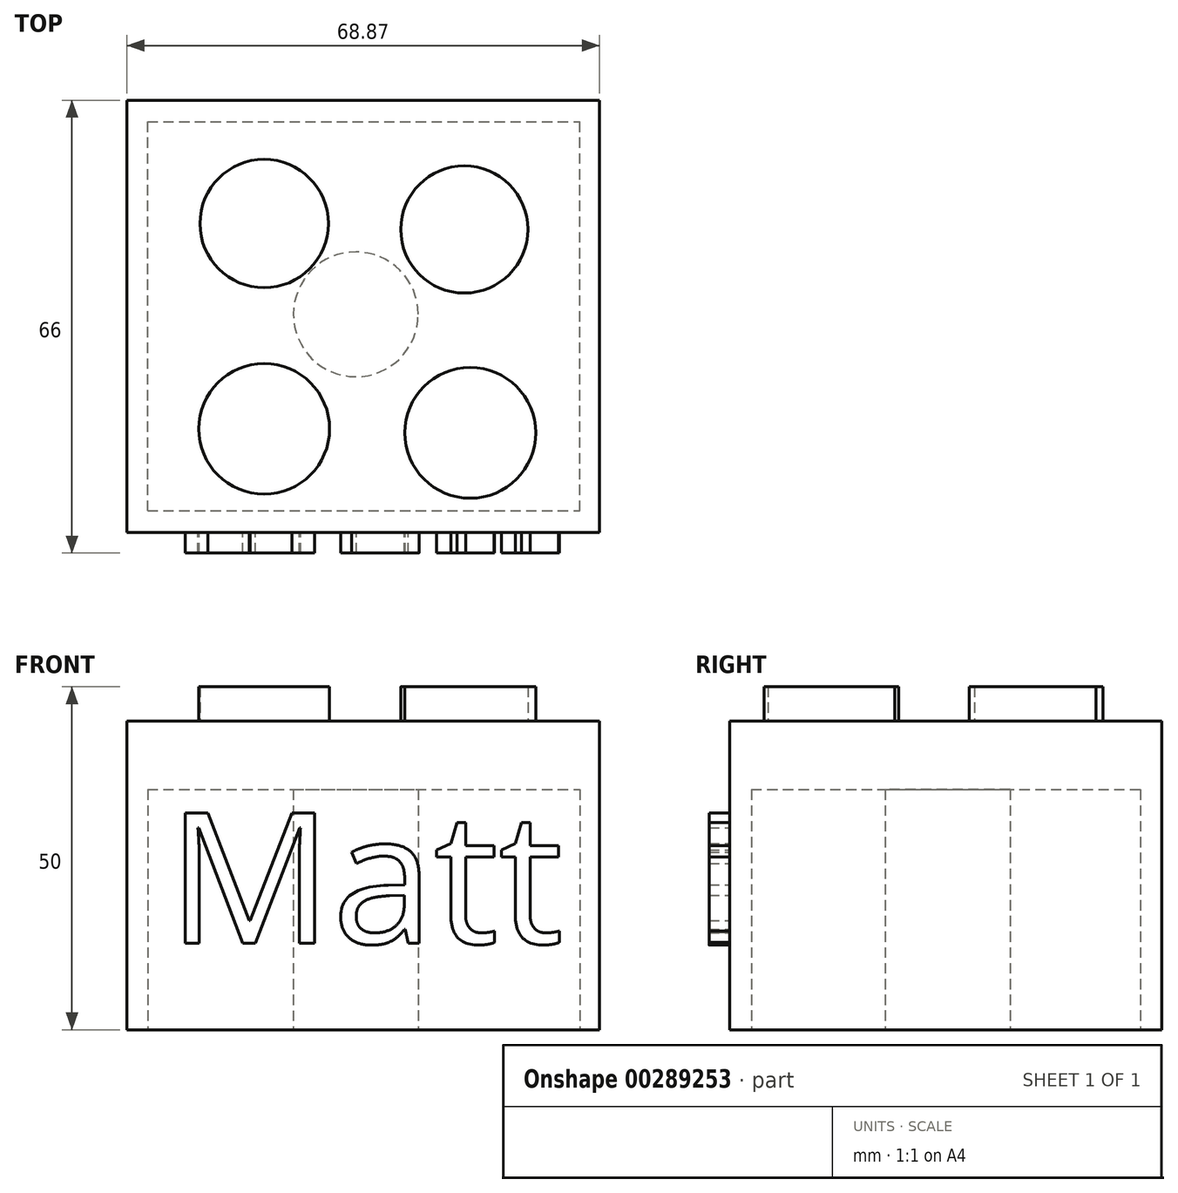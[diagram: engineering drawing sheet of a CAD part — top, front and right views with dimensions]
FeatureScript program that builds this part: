
annotation { "Feature Type Name" : "Feature", "Feature Type Description" : "" }
export const myFeature = defineFeature(function(context is Context, id is Id, definition is map)
    precondition{}
    {
        {
            var Q0;
            Q0=qCreatedBy(makeId("Top.planeOp"),FACE);
            var sketch = newSketch(context, id + "F0", { "sketchPlane" : qUnion([Q0])});
            skLineSegment(sketch, "E0.bottom", {"start": v(0, 0) * mm, "end": v(68.87, 0) * mm});
            skLineSegment(sketch, "E0.top", {"start": v(0, 63) * mm, "end": v(68.87, 63) * mm});
            skLineSegment(sketch, "E0.left", {"start": v(0, 0) * mm, "end": v(0, 63) * mm});
            skLineSegment(sketch, "E0.right", {"start": v(68.87, 0) * mm, "end": v(68.87, 63) * mm});
            skSolve(sketch);
        }
        {
            var Q0;
            Q0 = qSketchRegion(id + "F0", true);
            extrude(context, id + "F1", {"entities" : qUnion([Q0]), "depth" : 45 * mm});
        }
        {
            var Q0;
            Q0=makeQuery(id+"F1.opExtrude","CAP_FACE",FACE,{"disambiguationData":[OSD([sQuery(id+"F0.wireOp",EDGE,"E0.bottom"),sQuery(id+"F0.wireOp",EDGE,"E0.top"),sQuery(id+"F0.wireOp",EDGE,"E0.left"),sQuery(id+"F0.wireOp",EDGE,"E0.right")])],"isStart":false});
            var sketch = newSketch(context, id + "F2", { "sketchPlane" : qUnion([Q0])});
            skCircle(sketch, "E1", {"center": v(20, 45.03) * mm, "radius": 9.36 * mm});
            skCircle(sketch, "E2", {"center": v(49.18, 44.17) * mm, "radius": 9.27 * mm});
            skCircle(sketch, "E3", {"center": v(20, 15.1) * mm, "radius": 9.53 * mm});
            skCircle(sketch, "E4", {"center": v(50.05, 14.53) * mm, "radius": 9.54 * mm});
            skSolve(sketch);
        }
        {
            var Q0;
            Q0 = qSketchRegion(id + "F2", true);
            extrude(context, id + "F3", {"entities" : qUnion([Q0]), "operationType" : NewBodyOperationType.ADD, "depth" : 5 * mm});
        }
        {
            var Q0;
            Q0=makeQuery(id+"F1.opExtrude","CAP_FACE",FACE,{"disambiguationData":[OSD([sQuery(id+"F0.wireOp",EDGE,"E0.bottom"),sQuery(id+"F0.wireOp",EDGE,"E0.top"),sQuery(id+"F0.wireOp",EDGE,"E0.left"),sQuery(id+"F0.wireOp",EDGE,"E0.right")])],"isStart":true});
            var sketch = newSketch(context, id + "F4", { "sketchPlane" : qUnion([Q0])});
            skLineSegment(sketch, "E5.bottom", {"start": v(3, -3.15) * mm, "end": v(66, -3.15) * mm});
            skLineSegment(sketch, "E5.top", {"start": v(3, -59.85) * mm, "end": v(66, -59.85) * mm});
            skLineSegment(sketch, "E5.left", {"start": v(3, -3.15) * mm, "end": v(3, -59.85) * mm});
            skLineSegment(sketch, "E5.right", {"start": v(66, -3.15) * mm, "end": v(66, -59.85) * mm});
            skCircle(sketch, "E6", {"center": v(33.36, -31.8) * mm, "radius": 9.1 * mm});
            skSolve(sketch);
        }
        {
            var Q0;
            Q0 = qSketchRegion(id + "F4", true);
            extrude(context, id + "F5", {"entities" : qUnion([Q0]), "operationType" : NewBodyOperationType.REMOVE, "oppositeDirection" : true, "depth" : 35 * mm});
        }
        {
            var Q0;
            Q0=makeQuery(id+"F1.opExtrude","SWEPT_FACE",FACE,{"disambiguationData":[OSD([sQuery(id+"F0.wireOp",EDGE,"E0.bottom")])]});
            var sketch = newSketch(context, id + "F6", { "sketchPlane" : qUnion([Q0])});
            skText(sketch, "E7", { "text": "Matt\n", "fontName": "OpenSans-Regular.ttf"});
            const initialGuessF6  = {"E7": [0.00587, 0.0126, 1, 0, 0.01919]};
            skSetInitialGuess(sketch, initialGuessF6);
            skSolve(sketch);
        }
        {
            var Q0;
            Q0 = qSketchRegion(id + "F6", true);
            extrude(context, id + "F7", {"entities" : qUnion([Q0]), "operationType" : NewBodyOperationType.ADD, "depth" : 3 * mm});
        }
    });
